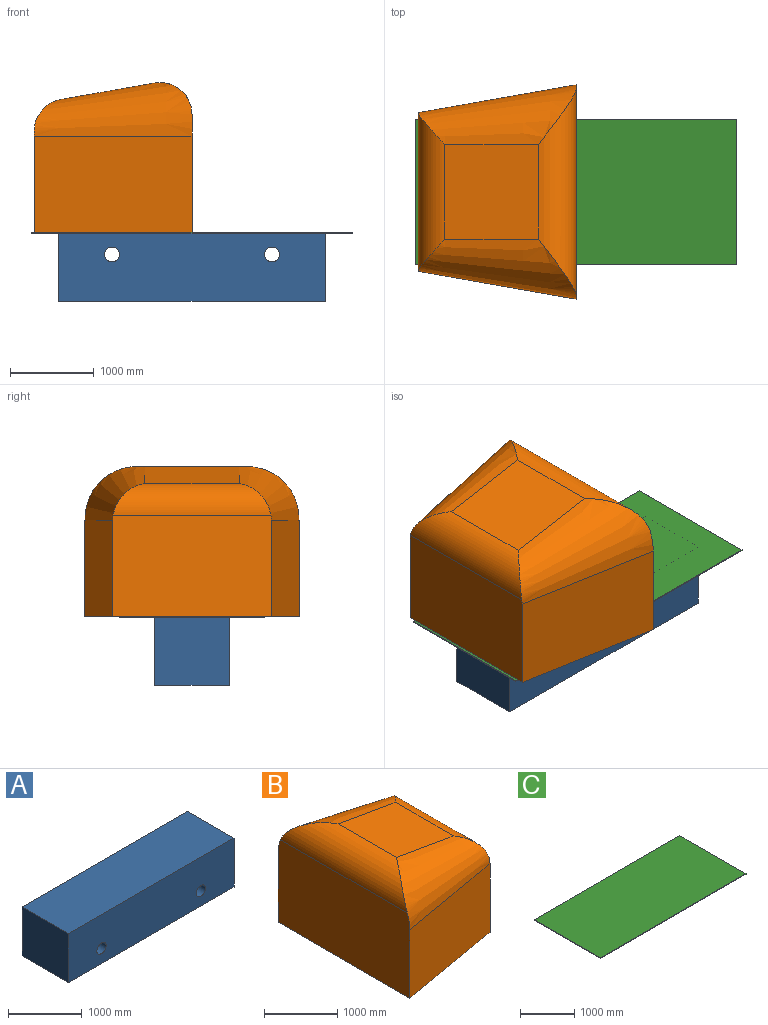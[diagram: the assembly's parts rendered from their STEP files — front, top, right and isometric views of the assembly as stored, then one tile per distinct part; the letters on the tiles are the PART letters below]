
ASSEMBLY  parts=3 mates=2
PART A: 8 faces, bbox 3175x889x812.8 mm
  f0: plane 3175x889mm, normal (0,0,1), area 2822575mm2, adj f1,f5,f6,f7
  f1: plane 889x812.8mm, normal (-1,0,0), area 722579.2mm2, adj f0,f2,f6,f7
  f2: plane 3175x889mm, normal (0,0,-1), area 2822575mm2, adj f1,f5,f6,f7
  f3: cylinder r=88.9mm len=889mm, axis (0,1,0), area 496573.3mm2, adj f6,f7
  f4: cylinder r=88.9mm len=889mm, axis (0,1,0), area 496573.3mm2, adj f6,f7
  f5: plane 889x812.8mm, normal (1,0,0), area 722579.2mm2, adj f0,f2,f6,f7
  f6: plane 3175x812.8mm, normal (0,-1,0), area 2530982.7mm2, adj f0,f1,f2,f3,f4,f5
  f7: plane 3175x812.8mm, normal (0,1,0), area 2530982.7mm2, adj f0,f1,f2,f3,f4,f5
PART B: 10 faces, bbox 1878.2x2549x1855.2 mm
  f0: plane 1878.19x1143mm, normal (0.17,0.98,0), area 2179882.8mm2, adj f1,f3,f5,f9
  f1: plane 2549.04x1401.12mm, normal (-1,0,0), area 3563282.4mm2, adj f0,f2,f5,f6,f8,f9
  f2: plane 1878.19x1143mm, normal (0.17,-0.98,0), area 2179882.8mm2, adj f1,f3,f8,f9
  f3: plane 1886.69x1204.3mm, normal (1,0,0), area 2271941.2mm2, adj f0,f2,f5,f7,f8,f9
  f4: plane 1124.69x1116.19mm, normal (0.17,0,0.98), area 1274725.3mm2, adj f5,f6,f7,f8
  f5: cone r=381mm half-angle=10deg, axis (-1,0,0), area 1426325.6mm2, adj f0,f1,f3,f4,f6,f7
  f6: cylinder r=381mm len=2452.19mm, axis (0,-1,0), area 1260679.2mm2, adj f1,f4,f5,f8
  f7: cylinder r=381mm len=1876.76mm, axis (0,1,0), area 843427.1mm2, adj f3,f4,f5,f8
  f8: cone r=381mm half-angle=10deg, axis (-1,0,0), area 1426314.7mm2, adj f1,f2,f3,f4,f6,f7
  f9: plane 2549.04x1878.19mm, normal (0,0,-1), area 4165555.6mm2, adj f0,f1,f2,f3
PART C: 6 faces, bbox 3810x1727.2x12 mm
  f0: plane 3810x12mm, normal (0,1,0), area 45720mm2, adj f1,f3,f4,f5
  f1: plane 1727.2x12mm, normal (-1,0,0), area 20726.4mm2, adj f0,f2,f4,f5
  f2: plane 3810x12mm, normal (0,-1,0), area 45720mm2, adj f1,f3,f4,f5
  f3: plane 1727.2x12mm, normal (1,0,0), area 20726.4mm2, adj f0,f2,f4,f5
  f4: plane 3810x1727.2mm, normal (0,0,1), area 6580632mm2, adj f0,f1,f2,f3
  f5: plane 3810x1727.2mm, normal (0,0,-1), area 6580632mm2, adj f0,f1,f2,f3
PLACE A rot(axis=(1,0,0),180deg) t=(-2761.89,2164.69,-1058.61)mm
PLACE B rot(axis=(0,0,-1),180deg) t=(-4349.39,735.06,-423.61)mm
PLACE C rot(axis=(1,0,0),180deg) t=(-6254.39,3472.79,-1046.61)mm
MATE fastened A.f2 <-> C.f4  axis (0,0,1) through (-4349.39,2609.19,-1058.61)mm
MATE fastened C.f5 <-> B.f9  axis (0,0,1) through (-4349.39,2609.19,-1046.61)mm
